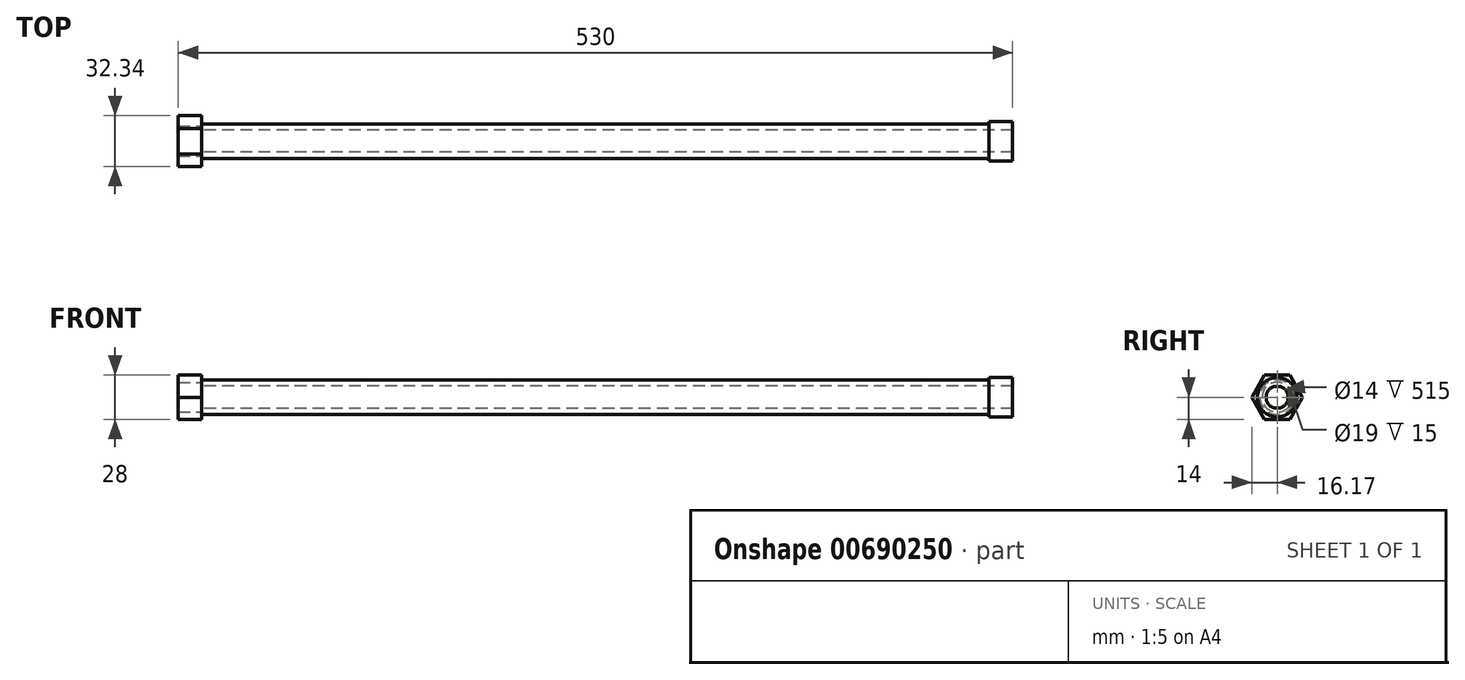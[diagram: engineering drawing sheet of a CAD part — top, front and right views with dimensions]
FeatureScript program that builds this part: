
annotation { "Feature Type Name" : "Feature", "Feature Type Description" : "" }
export const myFeature = defineFeature(function(context is Context, id is Id, definition is map)
    precondition{}
    {
        {
            var Q0;
            Q0=qCreatedBy(makeId("Right.planeOp"),FACE);
            var sketch = newSketch(context, id + "F0", { "sketchPlane" : qUnion([Q0])});
            skCircle(sketch, "E0", {"center": v(0, 0) * mm, "radius": 11 * mm});
            skCircle(sketch, "E1", {"center": v(0, 0) * mm, "radius": 7 * mm});
            skSolve(sketch);
        }
        {
            var Q0;
            Q0=qSketchRegion(id+"F0",true);
            extrude(context, id + "F1", {"entities" : qUnion([Q0]), "depth" : 500 * mm});
        }
        {
            var Q0;
            Q0=makeQuery(id+"F1.opExtrude","CAP_FACE",FACE,{"disambiguationData":[OSD([sQuery(id+"F0.wireOp",EDGE,"E0"),sQuery(id+"F0.wireOp",EDGE,"E1")])],"isStart":false});
            var sketch = newSketch(context, id + "F2", { "sketchPlane" : qUnion([Q0])});
            skCircle(sketch, "E2", {"center": v(0, 0) * mm, "radius": 7 * mm});
            skCircle(sketch, "E3", {"center": v(0, 0) * mm, "radius": 12.5 * mm});
            skSolve(sketch);
        }
        {
            var Q0;
            Q0=qSketchRegion(id+"F2",true);
            extrude(context, id + "F3", {"entities" : qUnion([Q0]), "operationType" : NewBodyOperationType.ADD, "depth" : 15 * mm, "offsetDistance" : 25 * mm});
        }
        {
            var Q0;
            Q0=makeQuery(id+"F1.opExtrude","CAP_FACE",FACE,{"disambiguationData":[OSD([sQuery(id+"F0.wireOp",EDGE,"E0"),sQuery(id+"F0.wireOp",EDGE,"E1")])],"isStart":true});
            var sketch = newSketch(context, id + "F4", { "sketchPlane" : qUnion([Q0])});
            skCircle(sketch, "E4", {"center": v(0, 0) * mm, "radius": 9.5 * mm});
            skCircle(sketch, "E5", {"center": v(0, 0) * mm, "radius": 14 * mm});
            skCircle(sketch, "E6.cCircle", {"center": v(0, 0) * mm, "radius": 14 * mm, "construction": true});
            skLineSegment(sketch, "E6.0", {"start": v(-8.08, 14) * mm, "end": v(8.08, 14) * mm});
            skLineSegment(sketch, "E6.1", {"start": v(8.08, 14) * mm, "end": v(16.17, 0) * mm});
            skLineSegment(sketch, "E6.2", {"start": v(16.17, 0) * mm, "end": v(8.08, -14) * mm});
            skLineSegment(sketch, "E6.3", {"start": v(8.08, -14) * mm, "end": v(-8.08, -14) * mm});
            skLineSegment(sketch, "E6.4", {"start": v(-8.08, -14) * mm, "end": v(-16.17, 0) * mm});
            skLineSegment(sketch, "E6.5", {"start": v(-16.17, 0) * mm, "end": v(-8.08, 14) * mm});
            skPoint(sketch, "E6.0.midPoint", {"position": v(0, 14) * mm});
            skSolve(sketch);
        }
        {
            var Q0;
            Q0=qSketchRegion(id+"F4",true);
            extrude(context, id + "F5", {"entities" : qUnion([Q0]), "operationType" : NewBodyOperationType.ADD, "depth" : 15 * mm});
        }
    });
